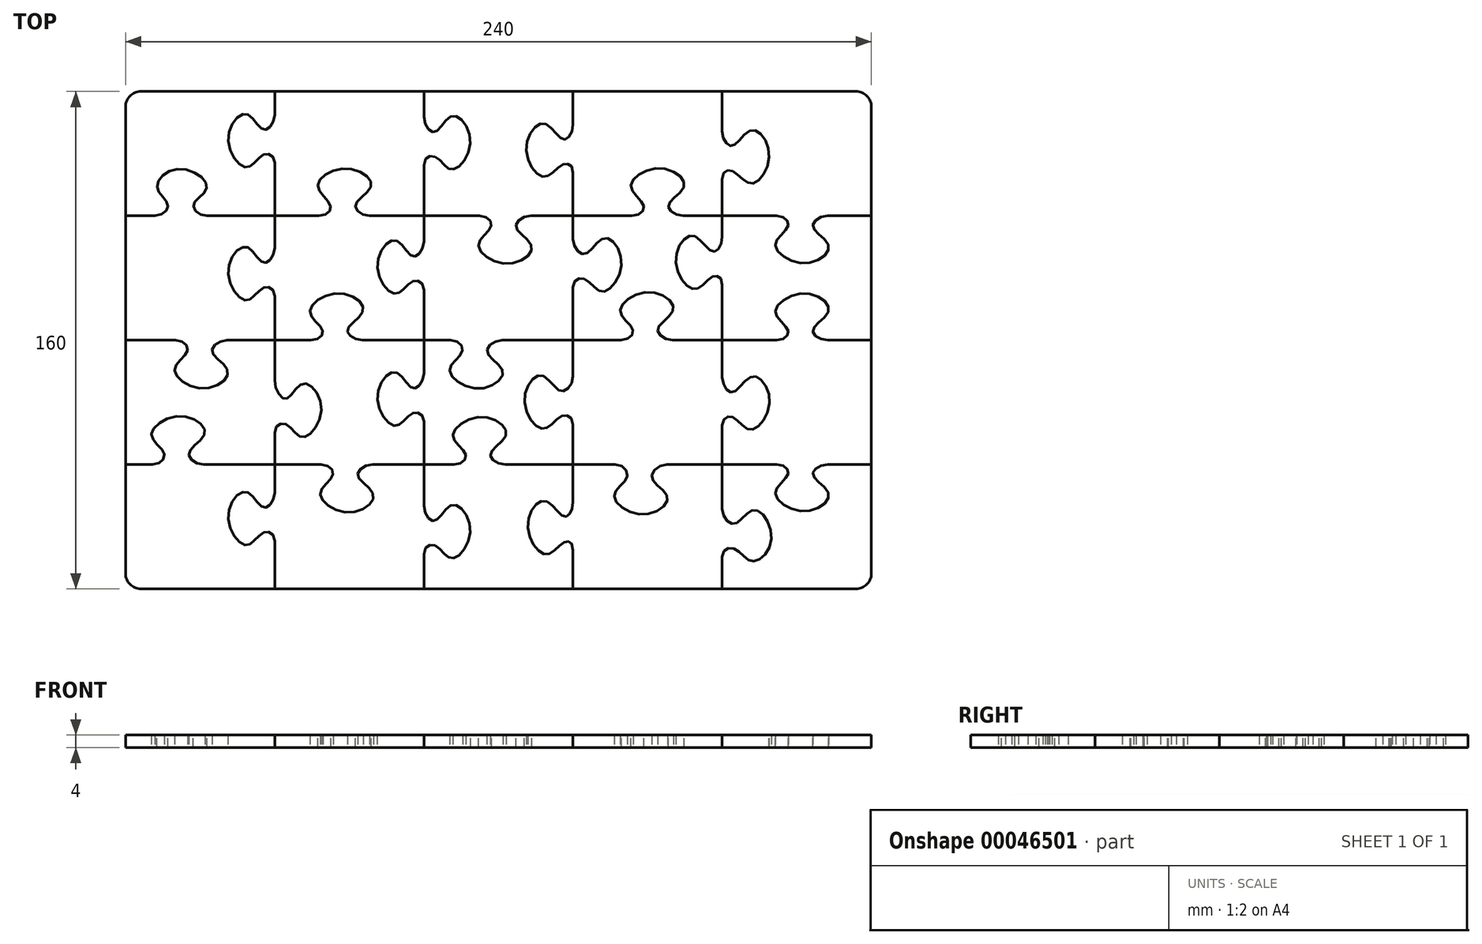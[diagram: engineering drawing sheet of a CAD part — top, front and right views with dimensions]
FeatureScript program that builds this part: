
annotation { "Feature Type Name" : "Feature", "Feature Type Description" : "" }
export const myFeature = defineFeature(function(context is Context, id is Id, definition is map)
    precondition{}
    {
        {
            var Q0;
            Q0=qCreatedBy(makeId("Top.planeOp"),FACE);
            var sketch = newSketch(context, id + "F0", { "sketchPlane" : qUnion([Q0])});
            skLineSegment(sketch, "E0.bottom", {"start": v(24, 0) * mm, "end": v(48, 0) * mm});
            skLineSegment(sketch, "E0.top", {"start": v(0, -80) * mm, "end": v(24, -80) * mm});
            skLineSegment(sketch, "E0.left", {"start": v(0, 0) * mm, "end": v(0, -20) * mm});
            skLineSegment(sketch, "E0.right", {"start": v(120, -20) * mm, "end": v(120, -40) * mm});
            skLineSegment(sketch, "E1", {"start": v(24, 0) * mm, "end": v(24, -3.76) * mm});
            skLineSegment(sketch, "E2", {"start": v(48, 0) * mm, "end": v(48, -4.1) * mm});
            skLineSegment(sketch, "E3", {"start": v(72, 0) * mm, "end": v(72, -5.3) * mm});
            skLineSegment(sketch, "E4", {"start": v(96, 0) * mm, "end": v(96, -6.37) * mm});
            skLineSegment(sketch, "E5", {"start": v(0, -20) * mm, "end": v(4.74, -20) * mm});
            skLineSegment(sketch, "E6", {"start": v(0, -40) * mm, "end": v(8.04, -40) * mm});
            skLineSegment(sketch, "E7", {"start": v(0, -60) * mm, "end": v(4.32, -60) * mm});
            skLineSegment(sketch, "E8.trimOffspring", {"start": v(48, -80) * mm, "end": v(72, -80) * mm});
            skLineSegment(sketch, "E9.trimOffspring", {"start": v(96, -80) * mm, "end": v(120, -80) * mm});
            skLineSegment(sketch, "E10.trimOffspring", {"start": v(72, 0) * mm, "end": v(96, 0) * mm});
            skLineSegment(sketch, "E11.trimOffspring", {"start": v(0, -40) * mm, "end": v(0, -60) * mm});
            skLineSegment(sketch, "E12.trimOffspring", {"start": v(120, -60) * mm, "end": v(120, -80) * mm});
            skLineSegment(sketch, "E13", {"start": v(0, 0) * mm, "end": v(24, 0) * mm});
            skLineSegment(sketch, "E14", {"start": v(48, 0) * mm, "end": v(72, 0) * mm});
            skLineSegment(sketch, "E15", {"start": v(96, 0) * mm, "end": v(120, 0) * mm});
            skLineSegment(sketch, "E16", {"start": v(120, 0) * mm, "end": v(120, -20) * mm});
            skLineSegment(sketch, "E17", {"start": v(120, -40) * mm, "end": v(120, -60) * mm});
            skLineSegment(sketch, "E18", {"start": v(96, -80) * mm, "end": v(72, -80) * mm});
            skLineSegment(sketch, "E19", {"start": v(48, -80) * mm, "end": v(24, -80) * mm});
            skLineSegment(sketch, "E20", {"start": v(0, -80) * mm, "end": v(0, -60) * mm});
            skLineSegment(sketch, "E21", {"start": v(0, -40) * mm, "end": v(0, -20) * mm});
            skPoint(sketch, "E22", {"position": v(24, -3.76) * mm});
            skPoint(sketch, "E23", {"position": v(24, -11.5) * mm});
            skPoint(sketch, "E24", {"position": v(13.12, -20) * mm});
            skLineSegment(sketch, "E25.trimOffspring", {"start": v(24, -11.5) * mm, "end": v(24, -25.13) * mm});
            skLineSegment(sketch, "E26.trimOffspring", {"start": v(13.12, -20) * mm, "end": v(31.09, -20) * mm});
            skLineSegment(sketch, "E27.trimOffspring", {"start": v(48, -11.84) * mm, "end": v(48, -24.09) * mm});
            skPoint(sketch, "E28", {"position": v(72, -5.3) * mm});
            skPoint(sketch, "E29", {"position": v(72, -13.05) * mm});
            skFitSpline(sketch, "E30", {"points": [v(72, -5.3) * mm, v(70.49, -7.71) * mm, v(67.37, -5.17) * mm, v(64.5, -9.08) * mm, v(67.37, -13.74) * mm, v(70.49, -11.69) * mm, v(72, -13.05) * mm], "startDerivative": vector(0, -25.43) * mm, "endDerivative": vector(0, -28.48) * mm});
            skLineSegment(sketch, "E31.trimOffspring", {"start": v(72, -13.05) * mm, "end": v(72, -23.74) * mm});
            skFitSpline(sketch, "E32.MirrorCS", {"points": [v(96, -6.37) * mm, v(97.54, -8.78) * mm, v(100.69, -6.24) * mm, v(103.55, -10.15) * mm, v(100.69, -14.81) * mm, v(97.54, -12.76) * mm, v(96, -14.12) * mm], "startDerivative": vector(0, -25.43) * mm, "endDerivative": vector(0, -28.48) * mm});
            skLineSegment(sketch, "E33.trimOffspring", {"start": v(96, -14.12) * mm, "end": v(96, -23.34) * mm});
            skFitSpline(sketch, "E34.MirrorCS", {"points": [v(96, -45.95) * mm, v(97.67, -48.36) * mm, v(100.85, -45.82) * mm, v(103.62, -49.73) * mm, v(100.57, -54.4) * mm, v(97.58, -52.33) * mm, v(96, -53.7) * mm], "startDerivative": vector(0, -25.43) * mm, "endDerivative": vector(0, -28.48) * mm});
            skFitSpline(sketch, "E35.MirrorCS", {"points": [v(96, -67.11) * mm, v(97.97, -69.53) * mm, v(101.07, -67.31) * mm, v(103.92, -71.8) * mm, v(100.87, -75.56) * mm, v(97.88, -73.5) * mm, v(96, -74.87) * mm], "startDerivative": vector(0, -25.43) * mm, "endDerivative": vector(0, -28.48) * mm});
            skFitSpline(sketch, "E36.MirrorCS", {"points": [v(48, -66.64) * mm, v(49.75, -69.05) * mm, v(52.5, -66.51) * mm, v(55.5, -70.42) * mm, v(52.5, -75.08) * mm, v(49.75, -73.02) * mm, v(48, -74.38) * mm], "startDerivative": vector(0, -25.43) * mm, "endDerivative": vector(0, -28.48) * mm});
            skFitSpline(sketch, "E37.MirrorCS", {"points": [v(24, -46.46) * mm, v(25.75, -49.44) * mm, v(28.5, -47) * mm, v(31.5, -50.92) * mm, v(28.5, -55.61) * mm, v(25.75, -53.5) * mm, v(24, -54.87) * mm], "startDerivative": vector(0, -25.28) * mm, "endDerivative": vector(0, -28.64) * mm});
            skFitSpline(sketch, "E38.MirrorCS", {"points": [v(72, -23.74) * mm, v(73.84, -26.15) * mm, v(77.02, -23.61) * mm, v(79.8, -27.52) * mm, v(76.74, -32.18) * mm, v(73.75, -30.12) * mm, v(72, -31.49) * mm], "startDerivative": vector(0, -25.43) * mm, "endDerivative": vector(0, -28.48) * mm});
            skFitSpline(sketch, "E39", {"points": [v(96, -23.34) * mm, v(94.5, -25.75) * mm, v(91.3, -23.21) * mm, v(88.54, -27.12) * mm, v(91.59, -31.78) * mm, v(94.58, -29.72) * mm, v(96, -31.09) * mm], "startDerivative": vector(0, -25.43) * mm, "endDerivative": vector(0, -28.48) * mm});
            skFitSpline(sketch, "E40", {"points": [v(72, -45.8) * mm, v(70.13, -48.22) * mm, v(66.94, -45.68) * mm, v(64.17, -49.59) * mm, v(67.23, -54.25) * mm, v(70.22, -52.2) * mm, v(72, -53.56) * mm], "startDerivative": vector(0, -25.43) * mm, "endDerivative": vector(0, -28.48) * mm});
            skFitSpline(sketch, "E41", {"points": [v(72, -66) * mm, v(70.68, -68.4) * mm, v(67.5, -65.87) * mm, v(64.73, -69.78) * mm, v(67.78, -74.44) * mm, v(70.77, -72.38) * mm, v(72, -73.75) * mm], "startDerivative": vector(0, -25.43) * mm, "endDerivative": vector(0, -28.48) * mm});
            skFitSpline(sketch, "E42", {"points": [v(48, -24.09) * mm, v(46.25, -26.52) * mm, v(43.5, -23.98) * mm, v(40.5, -27.89) * mm, v(43.5, -32.55) * mm, v(46.25, -30.5) * mm, v(48, -31.9) * mm], "startDerivative": vector(0, -25.43) * mm, "endDerivative": vector(0, -28.48) * mm});
            skFitSpline(sketch, "E43", {"points": [v(48, -45.31) * mm, v(46.25, -47.73) * mm, v(43.5, -45.2) * mm, v(40.5, -49.1) * mm, v(43.5, -53.77) * mm, v(46.25, -51.71) * mm, v(48, -53.1) * mm], "startDerivative": vector(0, -25.43) * mm, "endDerivative": vector(0, -28.48) * mm});
            skFitSpline(sketch, "E44", {"points": [v(24, -64.5) * mm, v(22.25, -66.93) * mm, v(19.5, -64.39) * mm, v(16.5, -68.3) * mm, v(19.5, -72.96) * mm, v(22.25, -70.9) * mm, v(24, -72.3) * mm], "startDerivative": vector(0, -25.43) * mm, "endDerivative": vector(0, -28.48) * mm});
            skFitSpline(sketch, "E45", {"points": [v(24, -25.13) * mm, v(22.25, -27.55) * mm, v(19.5, -25.01) * mm, v(16.5, -28.92) * mm, v(19.5, -33.59) * mm, v(22.25, -31.53) * mm, v(24, -32.92) * mm], "startDerivative": vector(0, -25.43) * mm, "endDerivative": vector(0, -28.48) * mm});
            skLineSegment(sketch, "E46.trimOffspring", {"start": v(96, -31.09) * mm, "end": v(96, -45.95) * mm});
            skLineSegment(sketch, "E47.trimOffspring", {"start": v(96, -53.7) * mm, "end": v(96, -67.11) * mm});
            skLineSegment(sketch, "E48.trimOffspring", {"start": v(96, -74.87) * mm, "end": v(96, -80) * mm});
            skLineSegment(sketch, "E49.trimOffspring", {"start": v(72, -31.49) * mm, "end": v(72, -45.8) * mm});
            skLineSegment(sketch, "E50.trimOffspring", {"start": v(48, -31.9) * mm, "end": v(48, -45.31) * mm});
            skFitSpline(sketch, "E51", {"points": [v(24, -3.76) * mm, v(22.25, -6.17) * mm, v(19.5, -3.63) * mm, v(16.5, -7.54) * mm, v(19.5, -12.2) * mm, v(22.25, -10.14) * mm, v(24, -11.5) * mm], "startDerivative": vector(0, -25.43) * mm, "endDerivative": vector(0, -28.48) * mm});
            skFitSpline(sketch, "E52.MirrorCS", {"points": [v(48, -4.1) * mm, v(49.75, -6.52) * mm, v(52.5, -3.98) * mm, v(55.5, -7.89) * mm, v(52.5, -12.56) * mm, v(49.75, -10.5) * mm, v(48, -11.84) * mm], "startDerivative": vector(0, -25.43) * mm, "endDerivative": vector(0, -28.48) * mm});
            skFitSpline(sketch, "E53.MirrorCS", {"points": [v(39.38, -20) * mm, v(36.97, -18.36) * mm, v(39.5, -15.17) * mm, v(35.6, -12.4) * mm, v(30.94, -15.17) * mm, v(33, -18.45) * mm, v(31.09, -20) * mm], "startDerivative": vector(-25.43, 0) * mm, "endDerivative": vector(-28.48, 0) * mm});
            skLineSegment(sketch, "E54.trimOffspring", {"start": v(39.28, -20) * mm, "end": v(56.92, -20) * mm});
            skFitSpline(sketch, "E55.MirrorCS", {"points": [v(13.12, -20) * mm, v(10.93, -18.22) * mm, v(13.08, -15.45) * mm, v(8.63, -12.45) * mm, v(5.08, -15.45) * mm, v(6.8, -18.25) * mm, v(4.58, -20) * mm], "startDerivative": vector(-25.43, 0) * mm, "endDerivative": vector(-28.48, -0.09) * mm});
            skLineSegment(sketch, "E56.trimOffspring", {"start": v(24, -32.92) * mm, "end": v(24, -46.46) * mm});
            skLineSegment(sketch, "E57.trimOffspring", {"start": v(24, -54.87) * mm, "end": v(24, -64.5) * mm});
            skLineSegment(sketch, "E58.trimOffspring", {"start": v(24, -72.3) * mm, "end": v(24, -80) * mm});
            skLineSegment(sketch, "E59.trimOffspring", {"start": v(48, -53.1) * mm, "end": v(48, -66.64) * mm});
            skLineSegment(sketch, "E60.trimOffspring", {"start": v(72, -53.56) * mm, "end": v(72, -66) * mm});
            skLineSegment(sketch, "E61.trimOffspring", {"start": v(48, -74.38) * mm, "end": v(48, -80) * mm});
            skLineSegment(sketch, "E62.trimOffspring", {"start": v(72, -73.75) * mm, "end": v(72, -80) * mm});
            skFitSpline(sketch, "E63.MirrorCS", {"points": [v(65.22, -20) * mm, v(62.8, -21.76) * mm, v(65.34, -24.95) * mm, v(61.44, -27.71) * mm, v(56.77, -24.66) * mm, v(58.83, -21.67) * mm, v(56.92, -20) * mm], "startDerivative": vector(-25.43, 0) * mm, "endDerivative": vector(-28.48, 0) * mm});
            skLineSegment(sketch, "E64.trimOffspring", {"start": v(65.22, -20) * mm, "end": v(81.45, -20) * mm});
            skFitSpline(sketch, "E65.MirrorCS", {"points": [v(88.01, -40) * mm, v(85.6, -38.26) * mm, v(88.14, -35.07) * mm, v(84.23, -32.3) * mm, v(79.57, -35.35) * mm, v(81.63, -38.34) * mm, v(79.72, -40) * mm], "startDerivative": vector(-25.43, 0) * mm, "endDerivative": vector(-28.48, 0) * mm});
            skFitSpline(sketch, "E66.MirrorCS", {"points": [v(61.12, -60) * mm, v(58.71, -58.32) * mm, v(61.25, -55.14) * mm, v(57.34, -52.37) * mm, v(52.68, -55.42) * mm, v(54.74, -58.41) * mm, v(52.83, -60) * mm], "startDerivative": vector(-25.43, 0) * mm, "endDerivative": vector(-28.48, 0) * mm});
            skFitSpline(sketch, "E67.MirrorCS", {"points": [v(113, -40) * mm, v(110.6, -38.42) * mm, v(113.13, -35.24) * mm, v(109.22, -32.47) * mm, v(104.56, -35.52) * mm, v(106.61, -38.51) * mm, v(104.7, -40) * mm], "startDerivative": vector(-25.43, 0) * mm, "endDerivative": vector(-28.48, 0) * mm});
            skFitSpline(sketch, "E68.MirrorCS", {"points": [v(12.62, -60) * mm, v(10.2, -58.17) * mm, v(12.74, -54.98) * mm, v(8.84, -52.22) * mm, v(4.17, -55.27) * mm, v(6.23, -58.26) * mm, v(4.32, -60) * mm], "startDerivative": vector(-25.43, 0) * mm, "endDerivative": vector(-28.48, 0) * mm});
            skFitSpline(sketch, "E69.MirrorCS", {"points": [v(38.1, -40) * mm, v(35.7, -38.4) * mm, v(38.23, -35.22) * mm, v(34.32, -32.45) * mm, v(29.66, -35.5) * mm, v(31.72, -38.5) * mm, v(29.8, -40) * mm], "startDerivative": vector(-25.43, 0) * mm, "endDerivative": vector(-28.48, 0) * mm});
            skFitSpline(sketch, "E70.MirrorCS", {"points": [v(113, -20) * mm, v(110.6, -21.7) * mm, v(113.13, -24.88) * mm, v(109.22, -27.65) * mm, v(104.56, -24.6) * mm, v(106.61, -21.6) * mm, v(104.7, -20) * mm], "startDerivative": vector(-25.43, 0) * mm, "endDerivative": vector(-28.48, 0) * mm});
            skFitSpline(sketch, "E71.MirrorCS", {"points": [v(113, -60) * mm, v(110.6, -61.56) * mm, v(113.13, -64.75) * mm, v(109.22, -67.52) * mm, v(104.56, -64.47) * mm, v(106.61, -61.48) * mm, v(104.7, -60) * mm], "startDerivative": vector(-25.43, 0) * mm, "endDerivative": vector(-28.48, 0) * mm});
            skFitSpline(sketch, "E72.MirrorCS", {"points": [v(87.07, -60) * mm, v(84.66, -62.07) * mm, v(87.2, -65.26) * mm, v(83.29, -68.03) * mm, v(78.62, -64.98) * mm, v(80.68, -61.98) * mm, v(78.77, -60) * mm], "startDerivative": vector(-25.43, 0) * mm, "endDerivative": vector(-28.48, 0) * mm});
            skFitSpline(sketch, "E73.MirrorCS", {"points": [v(60.58, -40) * mm, v(58.17, -41.84) * mm, v(60.7, -45.03) * mm, v(56.8, -47.8) * mm, v(52.13, -44.74) * mm, v(54.2, -41.75) * mm, v(52.28, -40) * mm], "startDerivative": vector(-25.43, 0) * mm, "endDerivative": vector(-28.48, 0) * mm});
            skFitSpline(sketch, "E74.MirrorCS", {"points": [v(39.76, -60) * mm, v(37.35, -61.73) * mm, v(39.89, -64.92) * mm, v(35.98, -67.69) * mm, v(31.32, -64.64) * mm, v(33.37, -61.64) * mm, v(31.47, -60) * mm], "startDerivative": vector(-25.43, 0) * mm, "endDerivative": vector(-28.48, 0) * mm});
            skFitSpline(sketch, "E75.MirrorCS", {"points": [v(16.33, -40) * mm, v(13.92, -41.8) * mm, v(16.46, -45) * mm, v(12.55, -47.76) * mm, v(7.89, -44.71) * mm, v(9.95, -41.72) * mm, v(8.04, -40) * mm], "startDerivative": vector(-25.43, 0) * mm, "endDerivative": vector(-28.48, 0) * mm});
            skFitSpline(sketch, "E76.MirrorCS", {"points": [v(89.75, -20) * mm, v(87.34, -18.32) * mm, v(89.88, -15.22) * mm, v(85.97, -12.36) * mm, v(81.3, -15.22) * mm, v(83.36, -18.4) * mm, v(81.45, -20) * mm], "startDerivative": vector(-25.43, 0) * mm, "endDerivative": vector(-28.48, 0) * mm});
            skLineSegment(sketch, "E77.trimOffspring", {"start": v(88.01, -40) * mm, "end": v(104.7, -40) * mm});
            skLineSegment(sketch, "E78.trimOffspring", {"start": v(12.62, -60) * mm, "end": v(31.47, -60) * mm});
            skLineSegment(sketch, "E79.trimOffspring", {"start": v(87.07, -60) * mm, "end": v(104.7, -60) * mm});
            skLineSegment(sketch, "E80.trimOffspring", {"start": v(113, -60) * mm, "end": v(120, -60) * mm});
            skLineSegment(sketch, "E81.trimOffspring", {"start": v(113, -40) * mm, "end": v(120, -40) * mm});
            skLineSegment(sketch, "E82.trimOffspring", {"start": v(113, -20) * mm, "end": v(120, -20) * mm});
            skLineSegment(sketch, "E83.trimOffspring", {"start": v(89.75, -20) * mm, "end": v(104.7, -20) * mm});
            skLineSegment(sketch, "E84.trimOffspring", {"start": v(60.58, -40) * mm, "end": v(79.72, -40) * mm});
            skLineSegment(sketch, "E85.trimOffspring", {"start": v(61.12, -60) * mm, "end": v(78.77, -60) * mm});
            skLineSegment(sketch, "E86.trimOffspring", {"start": v(39.76, -60) * mm, "end": v(52.83, -60) * mm});
            skLineSegment(sketch, "E87.trimOffspring", {"start": v(16.33, -40) * mm, "end": v(29.8, -40) * mm});
            skLineSegment(sketch, "E88.trimOffspring", {"start": v(38.1, -40) * mm, "end": v(52.28, -40) * mm});
            skPoint(sketch, "E89", {"position": v(96, -20) * mm});
            skPoint(sketch, "E90", {"position": v(96, -40) * mm});
            skPoint(sketch, "E91", {"position": v(96, -60) * mm});
            skPoint(sketch, "E92", {"position": v(72, -40) * mm});
            skPoint(sketch, "E93", {"position": v(72, -20) * mm});
            skPoint(sketch, "E94", {"position": v(48, -20) * mm});
            skPoint(sketch, "E95", {"position": v(48, -40) * mm});
            skPoint(sketch, "E96", {"position": v(72, -60) * mm});
            skPoint(sketch, "E97", {"position": v(48, -60) * mm});
            skPoint(sketch, "E98", {"position": v(24, -60) * mm});
            skPoint(sketch, "E99", {"position": v(24, -40) * mm});
            skPoint(sketch, "E100", {"position": v(24, -20) * mm});
            skLineSegment(sketch, "E101", {"start": v(19.5, 4.98) * mm, "end": v(19.5, -100.12) * mm, "construction": true});
            skLineSegment(sketch, "E102.MirrorCS", {"start": v(28.5, 4.98) * mm, "end": v(28.5, -100.12) * mm, "construction": true});
            skLineSegment(sketch, "E103", {"start": v(16.5, 3.9) * mm, "end": v(16.5, -100.12) * mm, "construction": true});
            skLineSegment(sketch, "E104.MirrorCS", {"start": v(31.5, 3.9) * mm, "end": v(31.5, -100.12) * mm, "construction": true});
            skLineSegment(sketch, "E105", {"start": v(22.25, 8.38) * mm, "end": v(22.25, -102.13) * mm, "construction": true});
            skLineSegment(sketch, "E106.MirrorCS", {"start": v(25.75, 8.38) * mm, "end": v(25.75, -102.13) * mm, "construction": true});
            skLineSegment(sketch, "E107", {"start": v(40.5, 11.95) * mm, "end": v(40.5, -92.06) * mm, "construction": true});
            skLineSegment(sketch, "E108", {"start": v(43.5, 13.04) * mm, "end": v(43.5, -92.06) * mm, "construction": true});
            skLineSegment(sketch, "E109", {"start": v(46.25, 16.44) * mm, "end": v(46.25, -94.07) * mm, "construction": true});
            skLineSegment(sketch, "E110.MirrorCS", {"start": v(49.75, 16.44) * mm, "end": v(49.75, -94.07) * mm, "construction": true});
            skLineSegment(sketch, "E111.MirrorCS", {"start": v(55.5, 11.95) * mm, "end": v(55.5, -92.06) * mm, "construction": true});
            skLineSegment(sketch, "E112.MirrorCS", {"start": v(52.5, 13.04) * mm, "end": v(52.5, -92.06) * mm, "construction": true});
            skSolve(sketch);
        }
        {
            var Q0;
            Q0=makeQuery(id+"F0.imprint","IMPRINT",FACE,{"disambiguationData":[TD([[makeQuery(id+"F0.imprint","IMPRINT",EDGE,{"derivedFrom":sQuery(id+"F0.wireOp",EDGE,"E0.left")}),1.0]])]});
            extrude(context, id + "F1", {"entities" : qUnion([Q0]), "depth" : 2 * mm});
        }
        {
            var Q0;
            Q0=makeQuery(id+"F0.imprint","IMPRINT",FACE,{"disambiguationData":[TD([[makeQuery(id+"F0.imprint","IMPRINT",EDGE,{"derivedFrom":sQuery(id+"F0.wireOp",EDGE,"E0.bottom")}),-1.0]])]});
            extrude(context, id + "F2", {"entities" : qUnion([Q0]), "depth" : 2 * mm});
        }
        {
            var Q0;
            Q0=makeQuery(id+"F0.imprint","IMPRINT",FACE,{"disambiguationData":[TD([[makeQuery(id+"F0.imprint","IMPRINT",EDGE,{"derivedFrom":sQuery(id+"F0.wireOp",EDGE,"E2")}),1.0]])]});
            extrude(context, id + "F3", {"entities" : qUnion([Q0]), "depth" : 2 * mm});
        }
        {
            var Q0;
            Q0=makeQuery(id+"F0.imprint","IMPRINT",FACE,{"disambiguationData":[TD([[makeQuery(id+"F0.imprint","IMPRINT",EDGE,{"derivedFrom":sQuery(id+"F0.wireOp",EDGE,"E3")}),1.0]])]});
            extrude(context, id + "F4", {"entities" : qUnion([Q0]), "depth" : 2 * mm});
        }
        {
            var Q0;
            Q0=makeQuery(id+"F0.imprint","IMPRINT",FACE,{"disambiguationData":[TD([[makeQuery(id+"F0.imprint","IMPRINT",EDGE,{"derivedFrom":sQuery(id+"F0.wireOp",EDGE,"E4")}),1.0]])]});
            extrude(context, id + "F5", {"entities" : qUnion([Q0]), "depth" : 2 * mm});
        }
        {
            var Q0;
            {var subQ0=sQuery(id+"F0.wireOp",EDGE,"E0.right");Q0=makeQuery(id+"F0.imprint","IMPRINT",FACE,{"disambiguationData":[TD([[makeQuery(id+"F0.imprint","IMPRINT",EDGE,{"derivedFrom":subQ0}),-1.0]])]});}
            extrude(context, id + "F6", {"entities" : qUnion([Q0]), "depth" : 2 * mm});
        }
        {
            var Q0;
            Q0=makeQuery(id+"F0.imprint","IMPRINT",FACE,{"disambiguationData":[TD([[makeQuery(id+"F0.imprint","IMPRINT",EDGE,{"derivedFrom":sQuery(id+"F0.wireOp",EDGE,"E9.trimOffspring")}),1.0]])]});
            extrude(context, id + "F7", {"entities" : qUnion([Q0]), "depth" : 2 * mm});
        }
        {
            var Q0;
            {var subQ7=sQuery(id+"F0.wireOp",EDGE,"E17");Q0=makeQuery(id+"F0.imprint","IMPRINT",FACE,{"disambiguationData":[TD([[makeQuery(id+"F0.imprint","IMPRINT",EDGE,{"derivedFrom":subQ7}),-1.0]])]});}
            extrude(context, id + "F8", {"entities" : qUnion([Q0]), "depth" : 2 * mm});
        }
        {
            var Q0;
            {var subQ3=sQuery(id+"F0.wireOp",EDGE,"E38.MirrorCS");Q0=makeQuery(id+"F0.imprint","IMPRINT",FACE,{"disambiguationData":[TD([[makeQuery(id+"F0.imprint","IMPRINT",EDGE,{"derivedFrom":subQ3}),1.0]])]});}
            extrude(context, id + "F9", {"entities" : qUnion([Q0]), "depth" : 2 * mm});
        }
        {
            var Q0;
            {var subQ3=sQuery(id+"F0.wireOp",EDGE,"E38.MirrorCS");Q0=makeQuery(id+"F0.imprint","IMPRINT",FACE,{"disambiguationData":[TD([[makeQuery(id+"F0.imprint","IMPRINT",EDGE,{"derivedFrom":subQ3}),-1.0]])]});}
            extrude(context, id + "F10", {"entities" : qUnion([Q0]), "depth" : 2 * mm});
        }
        {
            var Q0;
            {var subQ3=sQuery(id+"F0.wireOp",EDGE,"E5");Q0=makeQuery(id+"F0.imprint","IMPRINT",FACE,{"disambiguationData":[TD([[makeQuery(id+"F0.imprint","IMPRINT",EDGE,{"derivedFrom":subQ3}),-1.0]])]});}
            extrude(context, id + "F11", {"entities" : qUnion([Q0]), "depth" : 2 * mm});
        }
        {
            var Q0;
            {var subQ9=sQuery(id+"F0.wireOp",EDGE,"E42");Q0=makeQuery(id+"F0.imprint","IMPRINT",FACE,{"disambiguationData":[TD([[makeQuery(id+"F0.imprint","IMPRINT",EDGE,{"derivedFrom":subQ9}),-1.0]])]});}
            extrude(context, id + "F12", {"entities" : qUnion([Q0]), "depth" : 2 * mm});
        }
        {
            var Q0;
            {var subQ4=sQuery(id+"F0.wireOp",EDGE,"E11.trimOffspring");Q0=makeQuery(id+"F0.imprint","IMPRINT",FACE,{"disambiguationData":[TD([[makeQuery(id+"F0.imprint","IMPRINT",EDGE,{"derivedFrom":subQ4}),1.0]])]});}
            extrude(context, id + "F13", {"entities" : qUnion([Q0]), "depth" : 2 * mm});
        }
        {
            var Q0;
            Q0=makeQuery(id+"F0.imprint","IMPRINT",FACE,{"disambiguationData":[TD([[makeQuery(id+"F0.imprint","IMPRINT",EDGE,{"derivedFrom":sQuery(id+"F0.wireOp",EDGE,"E0.top")}),1.0]])]});
            extrude(context, id + "F14", {"entities" : qUnion([Q0]), "depth" : 2 * mm});
        }
        {
            var Q0;
            {var subQ6=sQuery(id+"F0.wireOp",EDGE,"E37.MirrorCS");Q0=makeQuery(id+"F0.imprint","IMPRINT",FACE,{"disambiguationData":[TD([[makeQuery(id+"F0.imprint","IMPRINT",EDGE,{"derivedFrom":subQ6}),1.0]])]});}
            extrude(context, id + "F15", {"entities" : qUnion([Q0]), "depth" : 2 * mm});
        }
        {
            var Q0;
            {var subQ7=sQuery(id+"F0.wireOp",EDGE,"E40");Q0=makeQuery(id+"F0.imprint","IMPRINT",FACE,{"disambiguationData":[TD([[makeQuery(id+"F0.imprint","IMPRINT",EDGE,{"derivedFrom":subQ7}),-1.0]])]});}
            extrude(context, id + "F16", {"entities" : qUnion([Q0]), "depth" : 2 * mm});
        }
        {
            var Q0;
            {var subQ3=sQuery(id+"F0.wireOp",EDGE,"E34.MirrorCS");Q0=makeQuery(id+"F0.imprint","IMPRINT",FACE,{"disambiguationData":[TD([[makeQuery(id+"F0.imprint","IMPRINT",EDGE,{"derivedFrom":subQ3}),-1.0]])]});}
            extrude(context, id + "F17", {"entities" : qUnion([Q0]), "depth" : 2 * mm});
        }
        {
            var Q0;
            Q0=makeQuery(id+"F0.imprint","IMPRINT",FACE,{"disambiguationData":[TD([[makeQuery(id+"F0.imprint","IMPRINT",EDGE,{"derivedFrom":sQuery(id+"F0.wireOp",EDGE,"E19")}),-1.0]])]});
            extrude(context, id + "F18", {"entities" : qUnion([Q0]), "depth" : 2 * mm});
        }
        {
            var Q0;
            Q0=makeQuery(id+"F0.imprint","IMPRINT",FACE,{"disambiguationData":[TD([[makeQuery(id+"F0.imprint","IMPRINT",EDGE,{"derivedFrom":sQuery(id+"F0.wireOp",EDGE,"E8.trimOffspring")}),1.0]])]});
            extrude(context, id + "F19", {"entities" : qUnion([Q0]), "depth" : 2 * mm});
        }
        {
            var Q0;
            Q0=makeQuery(id+"F0.imprint","IMPRINT",FACE,{"disambiguationData":[TD([[makeQuery(id+"F0.imprint","IMPRINT",EDGE,{"derivedFrom":sQuery(id+"F0.wireOp",EDGE,"E18")}),-1.0]])]});
            extrude(context, id + "F20", {"entities" : qUnion([Q0]), "depth" : 2 * mm});
        }
        {
            var Q0;
            Q0=makeQuery(id+"F7.opExtrude","SWEPT_BODY",BODY,{"disambiguationData":[OSD([sQuery(id+"F0.wireOp",EDGE,"E9.trimOffspring"),sQuery(id+"F0.wireOp",EDGE,"E12.trimOffspring"),sQuery(id+"F0.wireOp",EDGE,"E35.MirrorCS"),sQuery(id+"F0.wireOp",EDGE,"E47.trimOffspring"),sQuery(id+"F0.wireOp",EDGE,"E48.trimOffspring"),sQuery(id+"F0.wireOp",EDGE,"E71.MirrorCS"),sQuery(id+"F0.wireOp",EDGE,"E79.trimOffspring"),sQuery(id+"F0.wireOp",EDGE,"E80.trimOffspring")])]});
            var Q1;
            Q1=makeQuery(id+"F8.opExtrude","SWEPT_BODY",BODY,{"disambiguationData":[OSD([sQuery(id+"F0.wireOp",EDGE,"E17"),sQuery(id+"F0.wireOp",EDGE,"E34.MirrorCS"),sQuery(id+"F0.wireOp",EDGE,"E46.trimOffspring"),sQuery(id+"F0.wireOp",EDGE,"E47.trimOffspring"),sQuery(id+"F0.wireOp",EDGE,"E67.MirrorCS"),sQuery(id+"F0.wireOp",EDGE,"E71.MirrorCS"),sQuery(id+"F0.wireOp",EDGE,"E77.trimOffspring"),sQuery(id+"F0.wireOp",EDGE,"E79.trimOffspring"),sQuery(id+"F0.wireOp",EDGE,"E80.trimOffspring"),sQuery(id+"F0.wireOp",EDGE,"E81.trimOffspring")])]});
            var Q2;
            Q2=makeQuery(id+"F6.opExtrude","SWEPT_BODY",BODY,{"disambiguationData":[OSD([sQuery(id+"F0.wireOp",EDGE,"E0.right"),sQuery(id+"F0.wireOp",EDGE,"E33.trimOffspring"),sQuery(id+"F0.wireOp",EDGE,"E39"),sQuery(id+"F0.wireOp",EDGE,"E46.trimOffspring"),sQuery(id+"F0.wireOp",EDGE,"E67.MirrorCS"),sQuery(id+"F0.wireOp",EDGE,"E70.MirrorCS"),sQuery(id+"F0.wireOp",EDGE,"E77.trimOffspring"),sQuery(id+"F0.wireOp",EDGE,"E81.trimOffspring"),sQuery(id+"F0.wireOp",EDGE,"E82.trimOffspring"),sQuery(id+"F0.wireOp",EDGE,"E83.trimOffspring")])]});
            var Q3;
            Q3=makeQuery(id+"F5.opExtrude","SWEPT_BODY",BODY,{"disambiguationData":[OSD([sQuery(id+"F0.wireOp",EDGE,"E4"),sQuery(id+"F0.wireOp",EDGE,"E15"),sQuery(id+"F0.wireOp",EDGE,"E16"),sQuery(id+"F0.wireOp",EDGE,"E32.MirrorCS"),sQuery(id+"F0.wireOp",EDGE,"E33.trimOffspring"),sQuery(id+"F0.wireOp",EDGE,"E70.MirrorCS"),sQuery(id+"F0.wireOp",EDGE,"E82.trimOffspring"),sQuery(id+"F0.wireOp",EDGE,"E83.trimOffspring")])]});
            var Q4;
            Q4=makeQuery(id+"F4.opExtrude","SWEPT_BODY",BODY,{"disambiguationData":[OSD([sQuery(id+"F0.wireOp",EDGE,"E3"),sQuery(id+"F0.wireOp",EDGE,"E4"),sQuery(id+"F0.wireOp",EDGE,"E10.trimOffspring"),sQuery(id+"F0.wireOp",EDGE,"E30"),sQuery(id+"F0.wireOp",EDGE,"E31.trimOffspring"),sQuery(id+"F0.wireOp",EDGE,"E32.MirrorCS"),sQuery(id+"F0.wireOp",EDGE,"E33.trimOffspring"),sQuery(id+"F0.wireOp",EDGE,"E64.trimOffspring"),sQuery(id+"F0.wireOp",EDGE,"E76.MirrorCS"),sQuery(id+"F0.wireOp",EDGE,"E83.trimOffspring")])]});
            var Q5;
            Q5=makeQuery(id+"F20.opExtrude","SWEPT_BODY",BODY,{"disambiguationData":[OSD([sQuery(id+"F0.wireOp",EDGE,"E18"),sQuery(id+"F0.wireOp",EDGE,"E35.MirrorCS"),sQuery(id+"F0.wireOp",EDGE,"E41"),sQuery(id+"F0.wireOp",EDGE,"E47.trimOffspring"),sQuery(id+"F0.wireOp",EDGE,"E48.trimOffspring"),sQuery(id+"F0.wireOp",EDGE,"E60.trimOffspring"),sQuery(id+"F0.wireOp",EDGE,"E62.trimOffspring"),sQuery(id+"F0.wireOp",EDGE,"E72.MirrorCS"),sQuery(id+"F0.wireOp",EDGE,"E79.trimOffspring"),sQuery(id+"F0.wireOp",EDGE,"E85.trimOffspring")])]});
            var Q6;
            Q6=makeQuery(id+"F19.opExtrude","SWEPT_BODY",BODY,{"disambiguationData":[OSD([sQuery(id+"F0.wireOp",EDGE,"E8.trimOffspring"),sQuery(id+"F0.wireOp",EDGE,"E36.MirrorCS"),sQuery(id+"F0.wireOp",EDGE,"E41"),sQuery(id+"F0.wireOp",EDGE,"E59.trimOffspring"),sQuery(id+"F0.wireOp",EDGE,"E60.trimOffspring"),sQuery(id+"F0.wireOp",EDGE,"E61.trimOffspring"),sQuery(id+"F0.wireOp",EDGE,"E62.trimOffspring"),sQuery(id+"F0.wireOp",EDGE,"E66.MirrorCS"),sQuery(id+"F0.wireOp",EDGE,"E85.trimOffspring"),sQuery(id+"F0.wireOp",EDGE,"E86.trimOffspring")])]});
            var Q7;
            Q7=makeQuery(id+"F17.opExtrude","SWEPT_BODY",BODY,{"disambiguationData":[OSD([sQuery(id+"F0.wireOp",EDGE,"E34.MirrorCS"),sQuery(id+"F0.wireOp",EDGE,"E40"),sQuery(id+"F0.wireOp",EDGE,"E46.trimOffspring"),sQuery(id+"F0.wireOp",EDGE,"E47.trimOffspring"),sQuery(id+"F0.wireOp",EDGE,"E49.trimOffspring"),sQuery(id+"F0.wireOp",EDGE,"E60.trimOffspring"),sQuery(id+"F0.wireOp",EDGE,"E65.MirrorCS"),sQuery(id+"F0.wireOp",EDGE,"E72.MirrorCS"),sQuery(id+"F0.wireOp",EDGE,"E77.trimOffspring"),sQuery(id+"F0.wireOp",EDGE,"E79.trimOffspring"),sQuery(id+"F0.wireOp",EDGE,"E84.trimOffspring"),sQuery(id+"F0.wireOp",EDGE,"E85.trimOffspring")])]});
            var Q8;
            Q8=makeQuery(id+"F9.opExtrude","SWEPT_BODY",BODY,{"disambiguationData":[OSD([sQuery(id+"F0.wireOp",EDGE,"E31.trimOffspring"),sQuery(id+"F0.wireOp",EDGE,"E33.trimOffspring"),sQuery(id+"F0.wireOp",EDGE,"E38.MirrorCS"),sQuery(id+"F0.wireOp",EDGE,"E39"),sQuery(id+"F0.wireOp",EDGE,"E46.trimOffspring"),sQuery(id+"F0.wireOp",EDGE,"E49.trimOffspring"),sQuery(id+"F0.wireOp",EDGE,"E64.trimOffspring"),sQuery(id+"F0.wireOp",EDGE,"E65.MirrorCS"),sQuery(id+"F0.wireOp",EDGE,"E76.MirrorCS"),sQuery(id+"F0.wireOp",EDGE,"E77.trimOffspring"),sQuery(id+"F0.wireOp",EDGE,"E83.trimOffspring"),sQuery(id+"F0.wireOp",EDGE,"E84.trimOffspring")])]});
            var Q9;
            Q9=makeQuery(id+"F10.opExtrude","SWEPT_BODY",BODY,{"disambiguationData":[OSD([sQuery(id+"F0.wireOp",EDGE,"E27.trimOffspring"),sQuery(id+"F0.wireOp",EDGE,"E31.trimOffspring"),sQuery(id+"F0.wireOp",EDGE,"E38.MirrorCS"),sQuery(id+"F0.wireOp",EDGE,"E42"),sQuery(id+"F0.wireOp",EDGE,"E49.trimOffspring"),sQuery(id+"F0.wireOp",EDGE,"E50.trimOffspring"),sQuery(id+"F0.wireOp",EDGE,"E54.trimOffspring"),sQuery(id+"F0.wireOp",EDGE,"E63.MirrorCS"),sQuery(id+"F0.wireOp",EDGE,"E64.trimOffspring"),sQuery(id+"F0.wireOp",EDGE,"E73.MirrorCS"),sQuery(id+"F0.wireOp",EDGE,"E84.trimOffspring"),sQuery(id+"F0.wireOp",EDGE,"E88.trimOffspring")])]});
            var Q10;
            Q10=makeQuery(id+"F3.opExtrude","SWEPT_BODY",BODY,{"disambiguationData":[OSD([sQuery(id+"F0.wireOp",EDGE,"E2"),sQuery(id+"F0.wireOp",EDGE,"E3"),sQuery(id+"F0.wireOp",EDGE,"E14"),sQuery(id+"F0.wireOp",EDGE,"E27.trimOffspring"),sQuery(id+"F0.wireOp",EDGE,"E30"),sQuery(id+"F0.wireOp",EDGE,"E31.trimOffspring"),sQuery(id+"F0.wireOp",EDGE,"E52.MirrorCS"),sQuery(id+"F0.wireOp",EDGE,"E54.trimOffspring"),sQuery(id+"F0.wireOp",EDGE,"E63.MirrorCS"),sQuery(id+"F0.wireOp",EDGE,"E64.trimOffspring")])]});
            var Q11;
            Q11=makeQuery(id+"F16.opExtrude","SWEPT_BODY",BODY,{"disambiguationData":[OSD([sQuery(id+"F0.wireOp",EDGE,"E40"),sQuery(id+"F0.wireOp",EDGE,"E43"),sQuery(id+"F0.wireOp",EDGE,"E49.trimOffspring"),sQuery(id+"F0.wireOp",EDGE,"E50.trimOffspring"),sQuery(id+"F0.wireOp",EDGE,"E59.trimOffspring"),sQuery(id+"F0.wireOp",EDGE,"E60.trimOffspring"),sQuery(id+"F0.wireOp",EDGE,"E66.MirrorCS"),sQuery(id+"F0.wireOp",EDGE,"E73.MirrorCS"),sQuery(id+"F0.wireOp",EDGE,"E84.trimOffspring"),sQuery(id+"F0.wireOp",EDGE,"E85.trimOffspring"),sQuery(id+"F0.wireOp",EDGE,"E86.trimOffspring"),sQuery(id+"F0.wireOp",EDGE,"E88.trimOffspring")])]});
            var Q12;
            Q12=makeQuery(id+"F18.opExtrude","SWEPT_BODY",BODY,{"disambiguationData":[OSD([sQuery(id+"F0.wireOp",EDGE,"E19"),sQuery(id+"F0.wireOp",EDGE,"E36.MirrorCS"),sQuery(id+"F0.wireOp",EDGE,"E44"),sQuery(id+"F0.wireOp",EDGE,"E57.trimOffspring"),sQuery(id+"F0.wireOp",EDGE,"E58.trimOffspring"),sQuery(id+"F0.wireOp",EDGE,"E59.trimOffspring"),sQuery(id+"F0.wireOp",EDGE,"E61.trimOffspring"),sQuery(id+"F0.wireOp",EDGE,"E74.MirrorCS"),sQuery(id+"F0.wireOp",EDGE,"E78.trimOffspring"),sQuery(id+"F0.wireOp",EDGE,"E86.trimOffspring")])]});
            var Q13;
            Q13=makeQuery(id+"F15.opExtrude","SWEPT_BODY",BODY,{"disambiguationData":[OSD([sQuery(id+"F0.wireOp",EDGE,"E37.MirrorCS"),sQuery(id+"F0.wireOp",EDGE,"E43"),sQuery(id+"F0.wireOp",EDGE,"E50.trimOffspring"),sQuery(id+"F0.wireOp",EDGE,"E56.trimOffspring"),sQuery(id+"F0.wireOp",EDGE,"E57.trimOffspring"),sQuery(id+"F0.wireOp",EDGE,"E59.trimOffspring"),sQuery(id+"F0.wireOp",EDGE,"E69.MirrorCS"),sQuery(id+"F0.wireOp",EDGE,"E74.MirrorCS"),sQuery(id+"F0.wireOp",EDGE,"E78.trimOffspring"),sQuery(id+"F0.wireOp",EDGE,"E86.trimOffspring"),sQuery(id+"F0.wireOp",EDGE,"E87.trimOffspring"),sQuery(id+"F0.wireOp",EDGE,"E88.trimOffspring")])]});
            var Q14;
            Q14=makeQuery(id+"F12.opExtrude","SWEPT_BODY",BODY,{"disambiguationData":[OSD([sQuery(id+"F0.wireOp",EDGE,"E25.trimOffspring"),sQuery(id+"F0.wireOp",EDGE,"E26.trimOffspring"),sQuery(id+"F0.wireOp",EDGE,"E27.trimOffspring"),sQuery(id+"F0.wireOp",EDGE,"E42"),sQuery(id+"F0.wireOp",EDGE,"E45"),sQuery(id+"F0.wireOp",EDGE,"E50.trimOffspring"),sQuery(id+"F0.wireOp",EDGE,"E53.MirrorCS"),sQuery(id+"F0.wireOp",EDGE,"E54.trimOffspring"),sQuery(id+"F0.wireOp",EDGE,"E56.trimOffspring"),sQuery(id+"F0.wireOp",EDGE,"E69.MirrorCS"),sQuery(id+"F0.wireOp",EDGE,"E87.trimOffspring"),sQuery(id+"F0.wireOp",EDGE,"E88.trimOffspring")])]});
            var Q15;
            Q15=makeQuery(id+"F2.opExtrude","SWEPT_BODY",BODY,{"disambiguationData":[OSD([sQuery(id+"F0.wireOp",EDGE,"E0.bottom"),sQuery(id+"F0.wireOp",EDGE,"E1"),sQuery(id+"F0.wireOp",EDGE,"E2"),sQuery(id+"F0.wireOp",EDGE,"E25.trimOffspring"),sQuery(id+"F0.wireOp",EDGE,"E26.trimOffspring"),sQuery(id+"F0.wireOp",EDGE,"E27.trimOffspring"),sQuery(id+"F0.wireOp",EDGE,"E51"),sQuery(id+"F0.wireOp",EDGE,"E52.MirrorCS"),sQuery(id+"F0.wireOp",EDGE,"E53.MirrorCS"),sQuery(id+"F0.wireOp",EDGE,"E54.trimOffspring")])]});
            var Q16;
            Q16=makeQuery(id+"F14.opExtrude","SWEPT_BODY",BODY,{"disambiguationData":[OSD([sQuery(id+"F0.wireOp",EDGE,"E0.top"),sQuery(id+"F0.wireOp",EDGE,"E7"),sQuery(id+"F0.wireOp",EDGE,"E20"),sQuery(id+"F0.wireOp",EDGE,"E44"),sQuery(id+"F0.wireOp",EDGE,"E57.trimOffspring"),sQuery(id+"F0.wireOp",EDGE,"E58.trimOffspring"),sQuery(id+"F0.wireOp",EDGE,"E68.MirrorCS"),sQuery(id+"F0.wireOp",EDGE,"E78.trimOffspring")])]});
            var Q17;
            Q17=makeQuery(id+"F13.opExtrude","SWEPT_BODY",BODY,{"disambiguationData":[OSD([sQuery(id+"F0.wireOp",EDGE,"E6"),sQuery(id+"F0.wireOp",EDGE,"E7"),sQuery(id+"F0.wireOp",EDGE,"E11.trimOffspring"),sQuery(id+"F0.wireOp",EDGE,"E37.MirrorCS"),sQuery(id+"F0.wireOp",EDGE,"E56.trimOffspring"),sQuery(id+"F0.wireOp",EDGE,"E57.trimOffspring"),sQuery(id+"F0.wireOp",EDGE,"E68.MirrorCS"),sQuery(id+"F0.wireOp",EDGE,"E75.MirrorCS"),sQuery(id+"F0.wireOp",EDGE,"E78.trimOffspring"),sQuery(id+"F0.wireOp",EDGE,"E87.trimOffspring")])]});
            var Q18;
            Q18=makeQuery(id+"F11.opExtrude","SWEPT_BODY",BODY,{"disambiguationData":[OSD([sQuery(id+"F0.wireOp",EDGE,"E5"),sQuery(id+"F0.wireOp",EDGE,"E6"),sQuery(id+"F0.wireOp",EDGE,"E21"),sQuery(id+"F0.wireOp",EDGE,"E25.trimOffspring"),sQuery(id+"F0.wireOp",EDGE,"E26.trimOffspring"),sQuery(id+"F0.wireOp",EDGE,"E45"),sQuery(id+"F0.wireOp",EDGE,"E55.MirrorCS"),sQuery(id+"F0.wireOp",EDGE,"E56.trimOffspring"),sQuery(id+"F0.wireOp",EDGE,"E75.MirrorCS"),sQuery(id+"F0.wireOp",EDGE,"E87.trimOffspring")])]});
            var Q19;
            Q19=makeQuery(id+"F1.opExtrude","SWEPT_BODY",BODY,{"disambiguationData":[OSD([sQuery(id+"F0.wireOp",EDGE,"E0.left"),sQuery(id+"F0.wireOp",EDGE,"E1"),sQuery(id+"F0.wireOp",EDGE,"E5"),sQuery(id+"F0.wireOp",EDGE,"E13"),sQuery(id+"F0.wireOp",EDGE,"E25.trimOffspring"),sQuery(id+"F0.wireOp",EDGE,"E26.trimOffspring"),sQuery(id+"F0.wireOp",EDGE,"E51"),sQuery(id+"F0.wireOp",EDGE,"E55.MirrorCS")])]});
            var Q20;
            Q20=qCreatedBy(makeId("Origin.pointOp"),VERTEX);
            transform(context, id + "F21", {"entities" : qUnion([Q0, Q1, Q2, Q3, Q4, Q5, Q6, Q7, Q8, Q9, Q10, Q11, Q12, Q13, Q14, Q15, Q16, Q17, Q18, Q19]), "transformType" : TransformType.SCALE_UNIFORMLY, "scale" : 2, "makeCopy" : false, "scalePoint" : qUnion([Q20])});
        }
        {
            var Q0;
            Q0=makeQuery(id+"F14.opExtrude","SWEPT_EDGE",EDGE,{"disambiguationData":[OSD([sQuery(id+"F0.wireOp",EDGE,"E0.top"),sQuery(id+"F0.wireOp",EDGE,"E20")])]});
            var Q1;
            Q1=makeQuery(id+"F7.opExtrude","SWEPT_EDGE",EDGE,{"disambiguationData":[OSD([sQuery(id+"F0.wireOp",EDGE,"E9.trimOffspring"),sQuery(id+"F0.wireOp",EDGE,"E12.trimOffspring")])]});
            var Q2;
            Q2=makeQuery(id+"F5.opExtrude","SWEPT_EDGE",EDGE,{"disambiguationData":[OSD([sQuery(id+"F0.wireOp",EDGE,"E15"),sQuery(id+"F0.wireOp",EDGE,"E16")])]});
            var Q3;
            Q3=makeQuery(id+"F1.opExtrude","SWEPT_EDGE",EDGE,{"disambiguationData":[OSD([sQuery(id+"F0.wireOp",EDGE,"E0.left"),sQuery(id+"F0.wireOp",EDGE,"E13")])]});
            fillet(context, id + "F22", {"entities" : qUnion([Q0, Q1, Q2, Q3]), "radius" : 5 * mm, "allowEdgeOverflow" : false});
        }
    });
